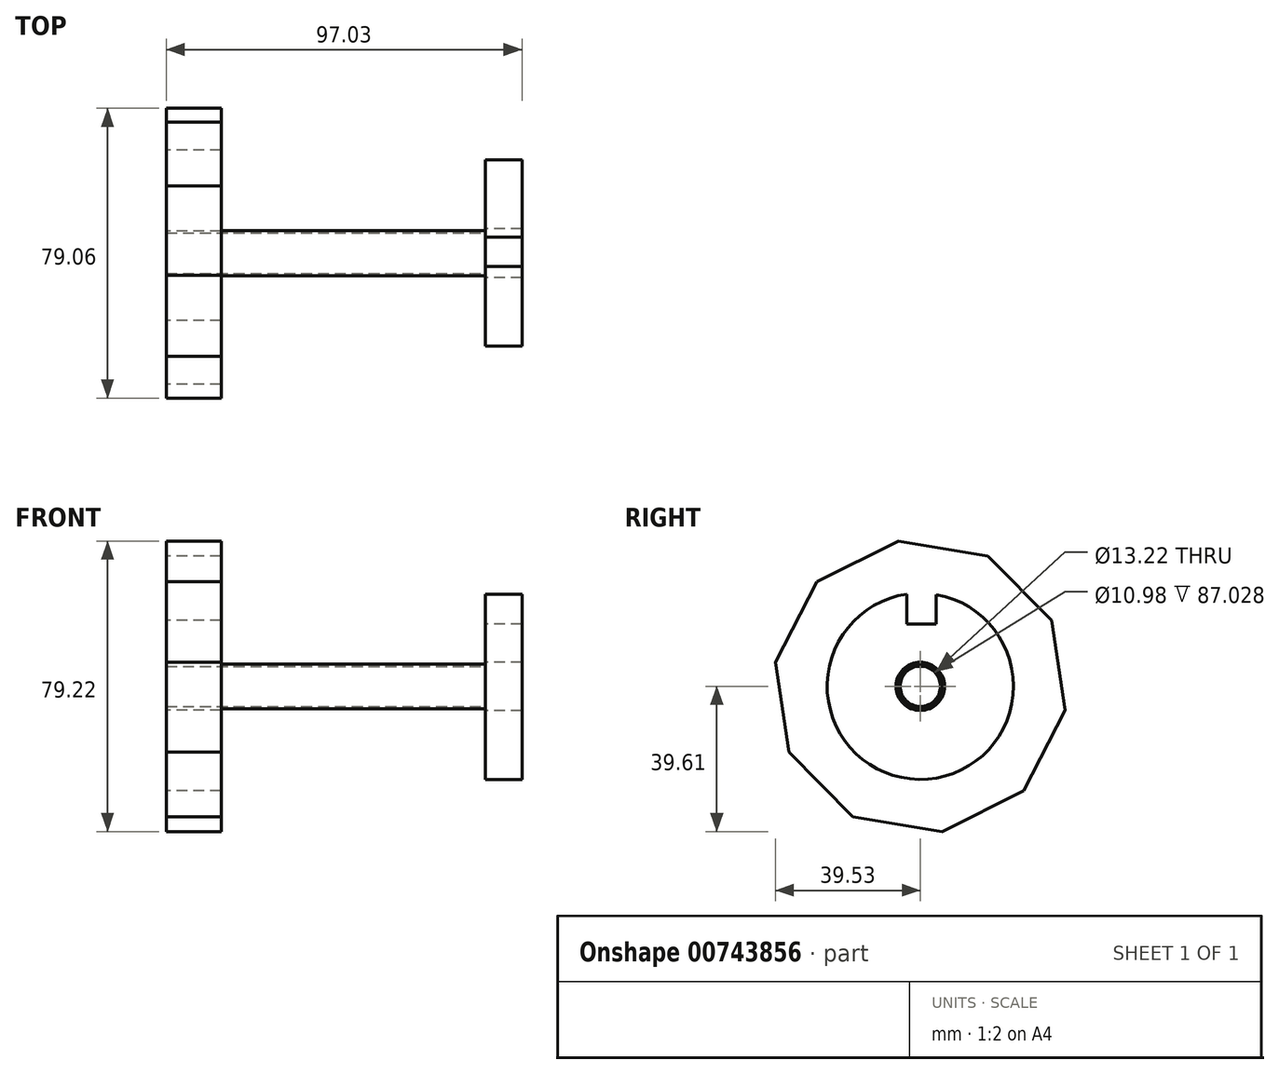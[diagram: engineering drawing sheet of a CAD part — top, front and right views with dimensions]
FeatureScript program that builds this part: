
annotation { "Feature Type Name" : "Feature", "Feature Type Description" : "" }
export const myFeature = defineFeature(function(context is Context, id is Id, definition is map)
    precondition{}
    {
        {
            var Q0;
            Q0=qCreatedBy(makeId("Right.planeOp"),FACE);
            var sketch = newSketch(context, id + "F0", { "sketchPlane" : qUnion([Q0])});
            skCircle(sketch, "E0.cCircle", {"center": v(0, 0) * mm, "radius": 38.1 * mm, "construction": true});
            skLineSegment(sketch, "E0.0", {"start": v(39.53, -6.5) * mm, "end": v(28.15, -28.5) * mm});
            skLineSegment(sketch, "E0.1", {"start": v(28.15, -28.5) * mm, "end": v(6.03, -39.6) * mm});
            skLineSegment(sketch, "E0.2", {"start": v(6.03, -39.6) * mm, "end": v(-18.4, -35.58) * mm});
            skLineSegment(sketch, "E0.3", {"start": v(-18.4, -35.58) * mm, "end": v(-35.8, -17.97) * mm});
            skLineSegment(sketch, "E0.4", {"start": v(-35.8, -17.97) * mm, "end": v(-39.53, 6.5) * mm});
            skLineSegment(sketch, "E0.5", {"start": v(-39.53, 6.5) * mm, "end": v(-28.15, 28.5) * mm});
            skLineSegment(sketch, "E0.6", {"start": v(-28.15, 28.5) * mm, "end": v(-6.03, 39.6) * mm});
            skLineSegment(sketch, "E0.7", {"start": v(-6.03, 39.6) * mm, "end": v(18.4, 35.58) * mm});
            skLineSegment(sketch, "E0.8", {"start": v(18.4, 35.58) * mm, "end": v(35.8, 17.97) * mm});
            skLineSegment(sketch, "E0.9", {"start": v(35.8, 17.97) * mm, "end": v(39.53, -6.5) * mm});
            skPoint(sketch, "E0.0.midPoint", {"position": v(33.84, -17.5) * mm});
            skSolve(sketch);
        }
        {
            var Q0;
            Q0=makeQuery(id+"F0.imprint","IMPRINT",FACE,{"disambiguationData":[TD([[makeQuery(id+"F0.imprint","IMPRINT",EDGE,{"derivedFrom":sQuery(id+"F0.wireOp",EDGE,"E0.0")}),-1.0]])]});
            extrude(context, id + "F1", {"entities" : qUnion([Q0]), "depth" : 15 * mm, "offsetDistance" : 25.4 * mm});
        }
        {
            var Q0;
            Q0=makeQuery(id+"F1.opExtrude","CAP_FACE",FACE,{"disambiguationData":[OSD([sQuery(id+"F0.wireOp",EDGE,"E0.0"),sQuery(id+"F0.wireOp",EDGE,"E0.1"),sQuery(id+"F0.wireOp",EDGE,"E0.2"),sQuery(id+"F0.wireOp",EDGE,"E0.3"),sQuery(id+"F0.wireOp",EDGE,"E0.4"),sQuery(id+"F0.wireOp",EDGE,"E0.5"),sQuery(id+"F0.wireOp",EDGE,"E0.6"),sQuery(id+"F0.wireOp",EDGE,"E0.7"),sQuery(id+"F0.wireOp",EDGE,"E0.8"),sQuery(id+"F0.wireOp",EDGE,"E0.9")])],"isStart":false});
            var sketch = newSketch(context, id + "F2", { "sketchPlane" : qUnion([Q0])});
            skCircle(sketch, "E1", {"center": v(0, 0) * mm, "radius": 5.49 * mm});
            skCircle(sketch, "E2", {"center": v(0, 0) * mm, "radius": 6.11 * mm});
            skSolve(sketch);
        }
        {
            var Q0;
            Q0=makeQuery(id+"F2.imprint","IMPRINT",FACE,{"disambiguationData":[TD([[makeQuery(id+"F2.imprint","IMPRINT",EDGE,{"derivedFrom":sQuery(id+"F2.wireOp",EDGE,"E1")}),1.0]])]});
            extrude(context, id + "F3", {"entities" : qUnion([Q0]), "operationType" : NewBodyOperationType.REMOVE, "oppositeDirection" : true, "depth" : 25.4 * mm, "offsetDistance" : 25.4 * mm});
        }
        {
            var Q0;
            Q0=makeQuery(id+"F2.imprint","IMPRINT",FACE,{"disambiguationData":[TD([[makeQuery(id+"F2.imprint","IMPRINT",EDGE,{"derivedFrom":sQuery(id+"F2.wireOp",EDGE,"E1")}),-1.0]])]});
            extrude(context, id + "F4", {"entities" : qUnion([Q0]), "operationType" : NewBodyOperationType.ADD, "depth" : 72.03 * mm, "offsetDistance" : 25.4 * mm});
        }
        {
            var Q0;
            Q0=makeQuery(id+"F4.opExtrude","CAP_FACE",FACE,{"disambiguationData":[OSD([sQuery(id+"F2.wireOp",EDGE,"E1"),sQuery(id+"F2.wireOp",EDGE,"E2")])],"isStart":false});
            var sketch = newSketch(context, id + "F5", { "sketchPlane" : qUnion([Q0])});
            skCircle(sketch, "E3", {"center": v(0, 0) * mm, "radius": 8.19 * mm});
            skCircle(sketch, "E4", {"center": v(0, 0) * mm, "radius": 6.1 * mm});
            skCircle(sketch, "E5.0", {"center": v(0, 0) * mm, "radius": 6.6 * mm});
            skSolve(sketch);
        }
        {
            var Q0;
            Q0=makeQuery(id+"F5.imprint","IMPRINT",FACE,{"disambiguationData":[TD([[makeQuery(id+"F5.imprint","IMPRINT",EDGE,{"derivedFrom":sQuery(id+"F5.wireOp",EDGE,"E3")}),1.0]])]});
            extrude(context, id + "F6", {"entities" : qUnion([Q0]), "depth" : 10 * mm, "offsetDistance" : 25.4 * mm});
        }
        {
            var Q0;
            Q0=makeQuery(id+"F6.opExtrude","SWEPT_BODY",BODY,{"disambiguationData":[OSD([sQuery(id+"F2.wireOp",EDGE,"E2"),sQuery(id+"F5.wireOp",EDGE,"E3")])]});
            deleteBodies(context, id + "F7", {"entities" : qUnion([Q0])});
        }
        {
            var Q0;
            Q0=makeQuery(id+"F4.opExtrude","CAP_FACE",FACE,{"disambiguationData":[OSD([sQuery(id+"F2.wireOp",EDGE,"E1"),sQuery(id+"F2.wireOp",EDGE,"E2")])],"isStart":false});
            var sketch = newSketch(context, id + "F8", { "sketchPlane" : qUnion([Q0])});
            skCircle(sketch, "E6", {"center": v(0, 0) * mm, "radius": 25.4 * mm});
            skLineSegment(sketch, "E7", {"start": v(-3.63, 25.14) * mm, "end": v(-3.63, 17.02) * mm});
            skLineSegment(sketch, "E8", {"start": v(-3.63, 17.02) * mm, "end": v(4.37, 17.02) * mm});
            skLineSegment(sketch, "E9", {"start": v(4.37, 17.02) * mm, "end": v(4.37, 25.02) * mm});
            skCircle(sketch, "E10", {"center": v(0, 0) * mm, "radius": 6.11 * mm});
            skCircle(sketch, "E11.0", {"center": v(0, 0) * mm, "radius": 6.61 * mm});
            skSolve(sketch);
        }
        {
            var Q0;
            {var subQ1=sQuery(id+"F8.wireOp",EDGE,"E7");Q0=makeQuery(id+"F8.imprint","IMPRINT",FACE,{"disambiguationData":[TD([[makeQuery(id+"F8.imprint","IMPRINT",EDGE,{"derivedFrom":subQ1}),-1.0]])]});}
            extrude(context, id + "F9", {"entities" : qUnion([Q0]), "depth" : 10 * mm, "offsetDistance" : 25.4 * mm});
        }
    });
